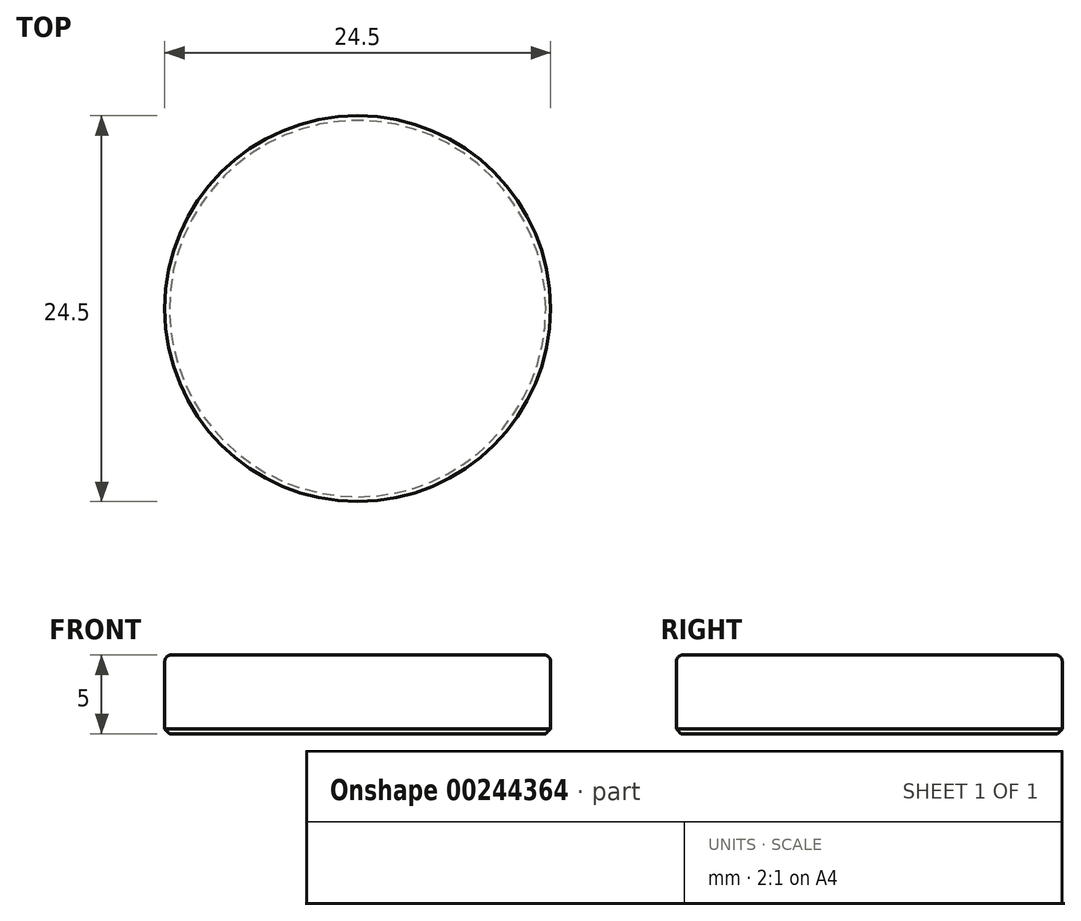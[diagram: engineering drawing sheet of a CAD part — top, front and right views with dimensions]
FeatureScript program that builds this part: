
annotation { "Feature Type Name" : "Feature", "Feature Type Description" : "" }
export const myFeature = defineFeature(function(context is Context, id is Id, definition is map)
    precondition{}
    {
        {
            var Q0;
            Q0=qCreatedBy(makeId("Top.planeOp"),FACE);
            var sketch = newSketch(context, id + "F0", { "sketchPlane" : qUnion([Q0])});
            skCircle(sketch, "E0", {"center": v(0, 0) * mm, "radius": 12.25 * mm});
            skSolve(sketch);
        }
        {
            var Q0;
            Q0=qSketchRegion(id+"F0",true);
            extrude(context, id + "F1", {"entities" : qUnion([Q0]), "depth" : 5 * mm});
        }
        {
            var Q0;
            Q0=makeQuery(id+"F1.opExtrude","CAP_EDGE",EDGE,{"disambiguationData":[OSD([sQuery(id+"F0.wireOp",EDGE,"E0")])],"isStart":false});
            fillet(context, id + "F2", {"entities" : qUnion([Q0]), "radius" : .4 * mm, "tangentPropagation" : true, "allowEdgeOverflow" : false});
        }
        {
            var Q0;
            Q0=makeQuery(id+"F1.opExtrude","CAP_EDGE",EDGE,{"disambiguationData":[OSD([sQuery(id+"F0.wireOp",EDGE,"E0")])],"isStart":true});
            chamfer(context, id + "F3", {"entities" : qUnion([Q0]), "width" : .3 * mm, "tangentPropagation" : true});
        }
    });
